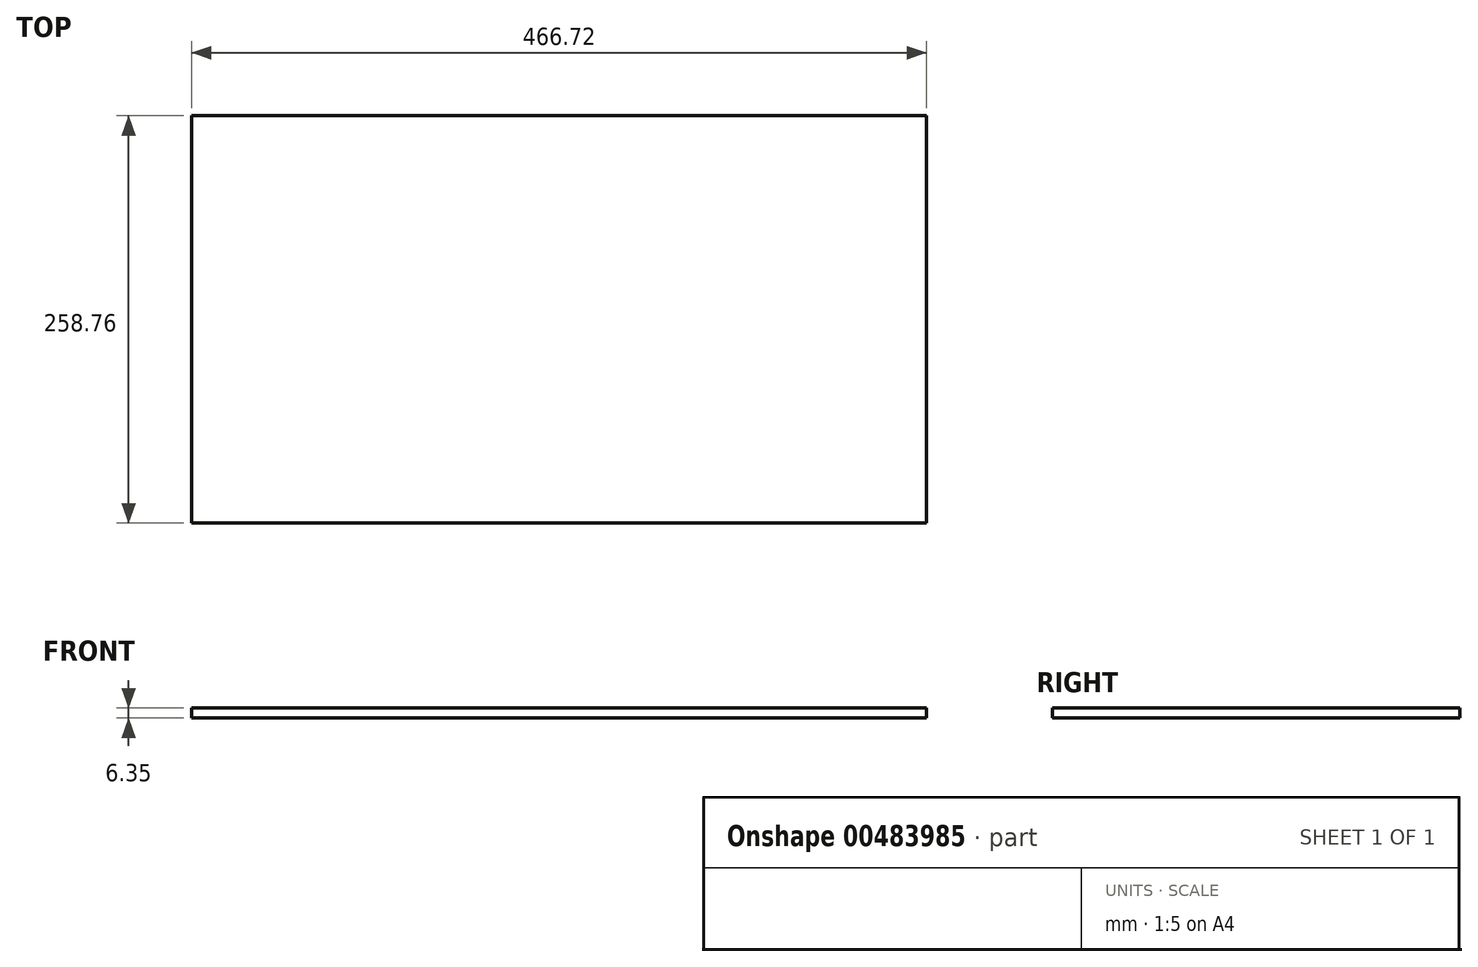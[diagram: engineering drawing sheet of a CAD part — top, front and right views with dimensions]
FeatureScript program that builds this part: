
annotation { "Feature Type Name" : "Feature", "Feature Type Description" : "" }
export const myFeature = defineFeature(function(context is Context, id is Id, definition is map)
    precondition{}
    {
        {
            var Q0;
            Q0=qCreatedBy(makeId("Top.planeOp"),FACE);
            var sketch = newSketch(context, id + "F0", { "sketchPlane" : qUnion([Q0])});
            skLineSegment(sketch, "E0.bottom", {"start": v(233.36, -129.38) * mm, "end": v(-233.36, -129.38) * mm});
            skLineSegment(sketch, "E0.top", {"start": v(233.36, 129.38) * mm, "end": v(-233.36, 129.38) * mm});
            skLineSegment(sketch, "E0.left", {"start": v(233.36, -129.38) * mm, "end": v(233.36, 129.38) * mm});
            skLineSegment(sketch, "E0.right", {"start": v(-233.36, -129.38) * mm, "end": v(-233.36, 129.38) * mm});
            skPoint(sketch, "E0.middle", {"position": v(0, 0) * mm});
            skSolve(sketch);
        }
        {
            var Q0;
            Q0 = qSketchRegion(id + "F0", true);
            extrude(context, id + "F1", {"entities" : qUnion([Q0]), "depth" : 6.35 * mm});
        }
    });
